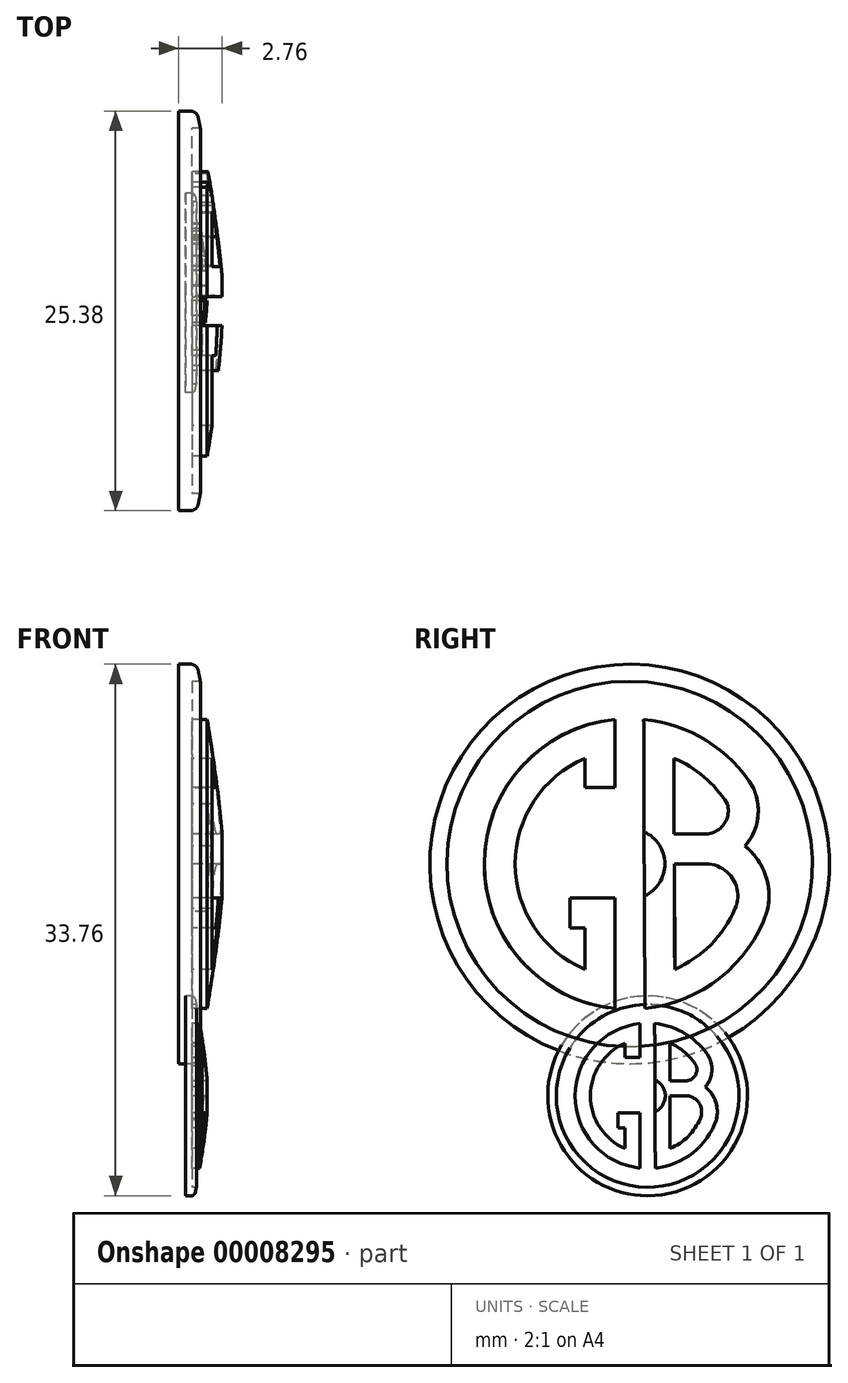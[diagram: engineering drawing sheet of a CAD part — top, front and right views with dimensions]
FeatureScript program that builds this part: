
annotation { "Feature Type Name" : "Feature", "Feature Type Description" : "" }
export const myFeature = defineFeature(function(context is Context, id is Id, definition is map)
    precondition{}
    {
        {
            var Q0;
            Q0=qCreatedBy(makeId("Right.planeOp"),FACE);
            var sketch = newSketch(context, id + "F0", { "sketchPlane" : qUnion([Q0])});
            skCircle(sketch, "E0", {"center": v(0, 0) * mm, "radius": 29.44 * mm});
            skCircle(sketch, "E1", {"center": v(0, 0) * mm, "radius": 26.92 * mm});
            skArc(sketch, "E2", {"start": v(-2.2, 21.31) * mm, "mid": v(-21.43, 0) * mm, "end": v(-2.2, -21.31) * mm});
            skArc(sketch, "E3", {"start": v(-6.62, 15.53) * mm, "mid": v(-16.88, 0) * mm, "end": v(-6.62, -15.53) * mm});
            skLineSegment(sketch, "E4.0", {"start": v(2.28, -29.46) * mm, "end": v(2.28, -29.35) * mm});
            skLineSegment(sketch, "E5.0", {"start": v(-2.2, -29.44) * mm, "end": v(-2.2, -29.36) * mm});
            skLineSegment(sketch, "E6.trimOffspring", {"start": v(2.25, -21.3) * mm, "end": v(2.07, 21.33) * mm});
            skLineSegment(sketch, "E7.trimOffspring", {"start": v(-2.2, -21.31) * mm, "end": v(-2.2, -4.98) * mm});
            skLineSegment(sketch, "E8.0", {"start": v(-6.62, -15.53) * mm, "end": v(-6.62, -9.4) * mm});
            skLineSegment(sketch, "E9", {"start": v(-6.62, 11.28) * mm, "end": v(-2.2, 11.28) * mm});
            skLineSegment(sketch, "E10.trimOffspring", {"start": v(-6.62, 11.28) * mm, "end": v(-6.62, 15.53) * mm});
            skLineSegment(sketch, "E11.trimOffspring", {"start": v(-2.2, 11.28) * mm, "end": v(-2.2, 21.31) * mm});
            skLineSegment(sketch, "E12.trimOffspring", {"start": v(-8.82, -9.4) * mm, "end": v(-8.82, -4.98) * mm});
            skLineSegment(sketch, "E13.trimOffspring", {"start": v(-6.62, -9.4) * mm, "end": v(-8.82, -9.4) * mm});
            skLineSegment(sketch, "E14.trimOffspring", {"start": v(-2.2, -4.98) * mm, "end": v(-8.82, -4.98) * mm});
            skArc(sketch, "E15.trimOffspring", {"start": v(6.64, -15.52) * mm, "mid": v(12.01, -11.86) * mm, "end": v(15.6, -6.45) * mm});
            skArc(sketch, "E16.trimOffspring", {"start": v(2.25, -21.3) * mm, "mid": v(13.33, -16.78) * mm, "end": v(20.25, -7) * mm});
            skArc(sketch, "E17", {"start": v(10.98, 4.42) * mm, "mid": v(13.84, 5.75) * mm, "end": v(14.37, 8.86) * mm});
            skPoint(sketch, "E17.first.point", {"position": v(14.37, 8.86) * mm});
            skPoint(sketch, "E17.second.point", {"position": v(7.94, 6.7) * mm});
            skPoint(sketch, "E17.third.point", {"position": v(10.98, 4.42) * mm});
            skArc(sketch, "E18.0", {"start": v(10.9, 0) * mm, "mid": v(11.2, 0) * mm, "end": v(11.49, 0) * mm});
            skLineSegment(sketch, "E19", {"start": v(18.59, 10.18) * mm, "end": v(18.26, 11.2) * mm});
            skPoint(sketch, "E20.second.point", {"position": v(11.04, -9.4) * mm});
            skPoint(sketch, "E20.third.point", {"position": v(15.6, -6.45) * mm});
            skArc(sketch, "E21.trimOffspring", {"start": v(14.37, 8.86) * mm, "mid": v(10.97, 12.83) * mm, "end": v(6.5, 15.57) * mm});
            skArc(sketch, "E22.trimOffspring", {"start": v(18.26, 11.2) * mm, "mid": v(11.35, 18.17) * mm, "end": v(2.07, 21.33) * mm});
            skArc(sketch, "E23.trimOffspring", {"start": v(19.2, -9.5) * mm, "mid": v(19.23, -9.45) * mm, "end": v(19.26, -9.4) * mm});
            skArc(sketch, "E24.trimOffspring", {"start": v(20.25, -7) * mm, "mid": v(20.05, -1.7) * mm, "end": v(16.98, 2.62) * mm});
            skArc(sketch, "E25.trimOffspring", {"start": v(15.55, -6.58) * mm, "mid": v(15.07, -1.97) * mm, "end": v(10.87, 0) * mm});
            skArc(sketch, "E26.trimOffspring", {"start": v(11.04, -9.4) * mm, "mid": v(11.23, -9.4) * mm, "end": v(11.42, -9.4) * mm});
            skLineSegment(sketch, "E27.trimOffspring", {"start": v(6.64, -15.52) * mm, "end": v(6.58, 0) * mm});
            skLineSegment(sketch, "E28.trimOffspring", {"start": v(11.6, 0) * mm, "end": v(6.58, 0) * mm});
            skArc(sketch, "E29.trimOffspring", {"start": v(16.98, 2.62) * mm, "mid": v(18.79, 6.2) * mm, "end": v(18.59, 10.18) * mm});
            skLineSegment(sketch, "E30.trimOffspring", {"start": v(11.31, 4.42) * mm, "end": v(6.56, 4.42) * mm});
            skLineSegment(sketch, "E31.trimOffspring", {"start": v(6.56, 4.42) * mm, "end": v(6.5, 15.57) * mm});
            skSolve(sketch);
        }
        {
            var Q0;
            Q0=makeQuery(id+"F0.imprint","IMPRINT",FACE,{"disambiguationData":[TD([[makeQuery(id+"F0.imprint","IMPRINT",EDGE,{"derivedFrom":sQuery(id+"F0.wireOp",EDGE,"E1")}),-1.0]])]});
            var Q1;
            Q1=makeQuery(id+"F0.imprint","IMPRINT",FACE,{"disambiguationData":[TD([[makeQuery(id+"F0.imprint","IMPRINT",EDGE,{"derivedFrom":sQuery(id+"F0.wireOp",EDGE,"E2")}),1.0]])]});
            var Q2;
            {var subQ19=sQuery(id+"F0.wireOp",EDGE,"E6.trimOffspring");Q2=makeQuery(id+"F0.imprint","IMPRINT",FACE,{"disambiguationData":[TD([[makeQuery(id+"F0.imprint","IMPRINT",EDGE,{"derivedFrom":subQ19}),-1.0]])]});}
            var Q3;
            Q3=sQuery(id+"F0.wireOp",EDGE,"E0");
            extrude(context, id + "F1", {"entities" : qUnion([Q0, Q1, Q2]), "surfaceEntities" : qUnion([Q3]), "depth" : 4.4 * mm});
        }
        {
            var Q0;
            Q0=qCreatedBy(makeId("Right.planeOp"),FACE);
            var sketch = newSketch(context, id + "F2", { "sketchPlane" : qUnion([Q0])});
            skCircle(sketch, "E32", {"center": v(0, 0) * mm, "radius": 29.44 * mm});
            skLineSegment(sketch, "E33", {"start": v(37.25, 0) * mm, "end": v(63.78, -1.45) * mm});
            skSolve(sketch);
        }
        {
            var Q0;
            Q0 = qSketchRegion(id + "F2", true);
            extrude(context, id + "F3", {"entities" : qUnion([Q0]), "oppositeDirection" : true, "depth" : 2 * mm});
        }
        {
            var Q0;
            Q0=makeQuery(id+"F1.opExtrude","SWEPT_BODY",BODY,{"disambiguationData":[OSD([sQuery(id+"F0.wireOp",EDGE,"E0"),sQuery(id+"F0.wireOp",EDGE,"E1")])]});
            var Q1;
            Q1=makeQuery(id+"F3.opExtrude","SWEPT_BODY",BODY,{"disambiguationData":[OSD([sQuery(id+"F2.wireOp",EDGE,"E32")])]});
            var Q2;
            Q2=makeQuery(id+"F1.opExtrude","SWEPT_BODY",BODY,{"disambiguationData":[OSD([sQuery(id+"F0.wireOp",EDGE,"E2"),sQuery(id+"F0.wireOp",EDGE,"E3"),sQuery(id+"F0.wireOp",EDGE,"E7.trimOffspring"),sQuery(id+"F0.wireOp",EDGE,"E8.0"),sQuery(id+"F0.wireOp",EDGE,"E9"),sQuery(id+"F0.wireOp",EDGE,"E10.trimOffspring"),sQuery(id+"F0.wireOp",EDGE,"E11.trimOffspring"),sQuery(id+"F0.wireOp",EDGE,"E12.trimOffspring"),sQuery(id+"F0.wireOp",EDGE,"E13.trimOffspring"),sQuery(id+"F0.wireOp",EDGE,"E14.trimOffspring")])]});
            var Q3;
            Q3=makeQuery(id+"F1.opExtrude","SWEPT_BODY",BODY,{"disambiguationData":[OSD([sQuery(id+"F0.wireOp",EDGE,"E6.trimOffspring"),sQuery(id+"F0.wireOp",EDGE,"E15.trimOffspring"),sQuery(id+"F0.wireOp",EDGE,"E16.trimOffspring"),sQuery(id+"F0.wireOp",EDGE,"E17"),sQuery(id+"F0.wireOp",EDGE,"E19"),sQuery(id+"F0.wireOp",EDGE,"E21.trimOffspring"),sQuery(id+"F0.wireOp",EDGE,"E22.trimOffspring"),sQuery(id+"F0.wireOp",EDGE,"E24.trimOffspring"),sQuery(id+"F0.wireOp",EDGE,"E25.trimOffspring"),sQuery(id+"F0.wireOp",EDGE,"E27.trimOffspring"),sQuery(id+"F0.wireOp",EDGE,"E28.trimOffspring"),sQuery(id+"F0.wireOp",EDGE,"E29.trimOffspring"),sQuery(id+"F0.wireOp",EDGE,"E30.trimOffspring"),sQuery(id+"F0.wireOp",EDGE,"E31.trimOffspring")])]});
            booleanBodies(context, id + "F4", {"operationType" : BooleanOperationType.UNION, "tools" : qUnion([Q0, Q1, Q2, Q3])});
        }
        {
            var Q0;
            Q0=qCreatedBy(makeId("Front.planeOp"),FACE);
            var sketch = newSketch(context, id + "F5", { "sketchPlane" : qUnion([Q0])});
            skLineSegment(sketch, "E34", {"start": v(-2.18, 29.72) * mm, "end": v(6.29, 29.72) * mm});
            skLineSegment(sketch, "E35", {"start": v(4.88, 0) * mm, "end": v(-14.49, 0) * mm, "construction": true});
            skLineSegment(sketch, "E36.trimOffspring", {"start": v(4.88, 0.04) * mm, "end": v(4.88, 31.06) * mm});
            skPoint(sketch, "E37.center.orphan", {"position": v(-88.03, 0) * mm});
            skLineSegment(sketch, "E38", {"start": v(4.43, 0.04) * mm, "end": v(4.88, 0.04) * mm});
            skArc(sketch, "E39", {"start": v(4.88, 0.04) * mm, "mid": v(3.2, 14.95) * mm, "end": v(0.63, 29.72) * mm});
            skSolve(sketch);
        }
        {
            var Q0;
            Q0 = qSketchRegion(id + "F5", true);
            var Q1;
            Q1=sQuery(id+"F5.wireOp",EDGE,"E35");
            revolve(context, id + "F6", {"operationType" : NewBodyOperationType.REMOVE, "entities" : qUnion([Q0]), "axis" : qUnion([Q1]), "revolveType" : RevolveType.FULL, "oppositeDirection" : true});
        }
        {
            var Q0;
            Q0=makeQuery(id+"F1.opExtrude","SWEPT_BODY",BODY,{"disambiguationData":[OSD([sQuery(id+"F0.wireOp",EDGE,"E0"),sQuery(id+"F0.wireOp",EDGE,"E1")])]});
            var Q1;
            Q1=sQuery(id+"F0.wireOp",VERTEX,"E1.center");
            transform(context, id + "F7", {"entities" : qUnion([Q0]), "transformType" : TransformType.SCALE_UNIFORMLY, "scale" : 0.43, "makeCopy" : false, "scalePoint" : qUnion([Q1])});
        }
        {
            var Q0;
            Q0=makeQuery(id+"F6.boolean.opBoolean","INTERSECT",EDGE,{"derivedFrom":[makeQuery(id+"F4.opBoolean","MERGE",FACE,{"derivedFrom":[makeQuery(id+"F1.opExtrude","SWEPT_FACE",FACE,{"disambiguationData":[OSD([sQuery(id+"F0.wireOp",EDGE,"E0")])]}),makeQuery(id+"F3.opExtrude","SWEPT_FACE",FACE,{"disambiguationData":[OSD([sQuery(id+"F2.wireOp",EDGE,"E32")])]})]}),makeQuery(id+"F6.opRevolve","SWEPT_FACE",FACE,{"disambiguationData":[OSD([sQuery(id+"F5.wireOp",EDGE,"E39")])]})]});
            fillet(context, id + "F8", {"entities" : qUnion([Q0]), "radius" : .5 * mm, "tangentPropagation" : true, "allowEdgeOverflow" : false});
        }
        {
            var Q0;
            Q0=makeQuery(id+"F1.opExtrude","SWEPT_BODY",BODY,{"disambiguationData":[OSD([sQuery(id+"F0.wireOp",EDGE,"E0"),sQuery(id+"F0.wireOp",EDGE,"E1")])]});
            var Q1;
            Q1=sQuery(id+"F0.wireOp",VERTEX,"E4.0.start");
            transform(context, id + "F9", {"entities" : qUnion([Q0]), "transformType" : TransformType.SCALE_UNIFORMLY, "scale" : 0.5, "makeCopy" : true, "scalePoint" : qUnion([Q1])});
        }
    });
